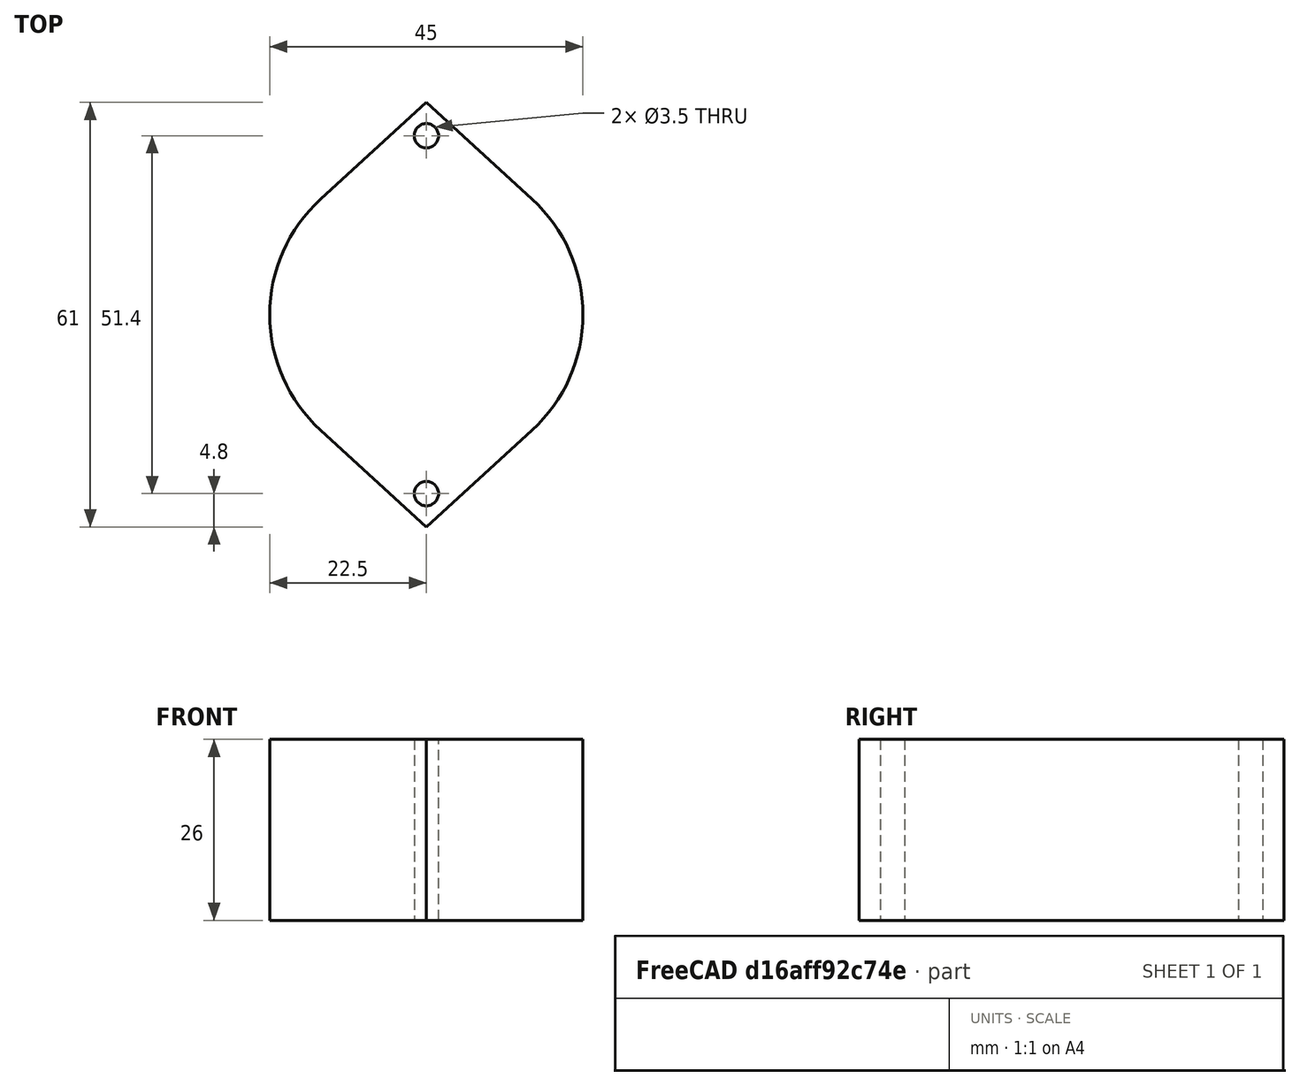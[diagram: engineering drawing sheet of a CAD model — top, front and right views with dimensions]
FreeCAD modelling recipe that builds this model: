
FCSTD DOCUMENT  (FreeCAD 0.21R33668 +7 (Git))
Label: speaker
License: All rights reserved
LicenseURL: http://en.wikipedia.org/wiki/All_rights_reserved
objects: Sketcher::SketchObject×1, PartDesign::Pad×1, PartDesign::Body×1, PartDesign::CoordinateSystem×1, App::Part×1
note: 5 computed .brp shape members not serialized (recipe doc carries the construction recipe); baked Part::Feature solids carry a one-line shape summary decoded from their .brp

FEATURE [Sketcher::SketchObject] Sketch
  FullyConstrained = false
  MapMode = 5
  Support = -> [XY_Plane]
  sketch-geometry (8):
    g0: Circle CenterX=0 CenterY=25.7 CenterZ=0 NormalX=0 NormalY=0 NormalZ=1 AngleXU=0 Radius=1.75
    g1: Circle CenterX=0 CenterY=-25.7 CenterZ=0 NormalX=0 NormalY=0 NormalZ=1 AngleXU=0 Radius=1.75
    g2: LineSegment StartX=0 StartY=30.5 StartZ=0 EndX=-15.1903 EndY=16.5984 EndZ=0
    g3: LineSegment StartX=0 StartY=30.5 StartZ=0 EndX=15.1903 EndY=16.5984 EndZ=0
    g4: LineSegment StartX=0 StartY=-30.5 StartZ=0 EndX=-15.1925 EndY=-16.5963 EndZ=0
    g5: LineSegment StartX=0 StartY=-30.5 StartZ=0 EndX=15.1903 EndY=-16.5984 EndZ=0
    g6: ArcOfCircle CenterX=0 CenterY=0 CenterZ=0 NormalX=0 NormalY=0 NormalZ=1 AngleXU=0 Radius=22.5 StartAngle=2.31193 EndAngle=3.97112
    g7: ArcOfCircle CenterX=0 CenterY=0 CenterZ=0 NormalX=0 NormalY=0 NormalZ=1 AngleXU=0 Radius=22.5 StartAngle=5.45352 EndAngle=7.11285
  constraints (6):
    c: Coincident(g4,g6)
    c: Coincident(g4,g5)
    c: Coincident(g5,g7)
    c: Coincident(g3,g7)
    c: Coincident(g2,g3)
    c: Coincident(g2,g6)
FEATURE [PartDesign::Pad] Pad
  Direction = (0,0,1)
  Length = 26
  Length2 = 10
  Profile = -> Sketch
  ReferenceAxis = -> Sketch [N_Axis]
  Type = 0
FEATURE [PartDesign::Body] Body
  Group = -> [Sketch,Pad]
  Origin = -> Origin
  Tip = -> Pad
FEATURE [PartDesign::CoordinateSystem] LCS_0
  AttacherType = Attacher::AttachEngine3D
  MapMode = 2
  Support = -> [X_Axis001]
FEATURE [App::Part] speaker
  Group = -> [LCS_0,Body]
  Origin = -> Origin001
